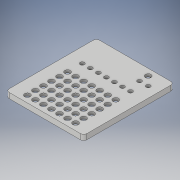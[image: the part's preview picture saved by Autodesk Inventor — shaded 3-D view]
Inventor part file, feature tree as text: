
AUTODESK INVENTOR PART (.ipt)
format: ipt  version: 2018.3 (Build 223284000, 284)  size: 318,464 bytes
history: native  units: in
note: dims shown in document units (in); Inventor stores cm internally (conversion verified against a paired STEP export)
features: extrude x5, sketch x3, fillet x1, projected_geometry x1
ambient origin geometry x8: Origin, YZ Plane, XZ Plane, XY Plane, X Axis, Y Axis, Z Axis, Center Point
bodies: Solid1 (feature_tree)
feature tree (10):
  sketch  "Sketch1"  dims[d0=2.7in d1=3.175in]
  extrude  "Extrusion1"  Depth=3.175in
  extrude  "Extrusion2"  Depth=0.1in
  extrude  "Extrusion3"  Depth=0.125in
  sketch  "Sketch3"  dims[d4=0.0591in d5=2.25in d6=2.4in d7=2.875in d9=0.15in d10=0.15in d11=0.15in d12=0.126in d13=0.1969in d14=0.1in d15=0.0in d16=0.1in d17=0.0in d18=2.3622in d20=0.3in d21=2.7559in d23=0.3in d26=0.2087in d27=2.7559in d29=0.3in d30=0.3937in d32=1.0in d34=0.3in d35=0.3in d36=2.4in d37=0.826in d38=0.1575in d40=0.39in d41=0.325in d42=0.324in d43=0.05in d44=0.0in d46=0.343in d47=0.05in d48=0.0in d49=0.304in d50=0.06in d51=0.05in d52=0.0in d53=0.1in d54=0.125in]
  extrude  "Extrusion4"  Depth=0.125in
  extrude  "Extrusion5"  Depth=0.125in
  fillet  "Fillet1"  Radius=0.15in
  sketch  "Sketch2"  dims[d2=0.1in d3=0.1in]
  projected_geometry  "Projected Loop1"
